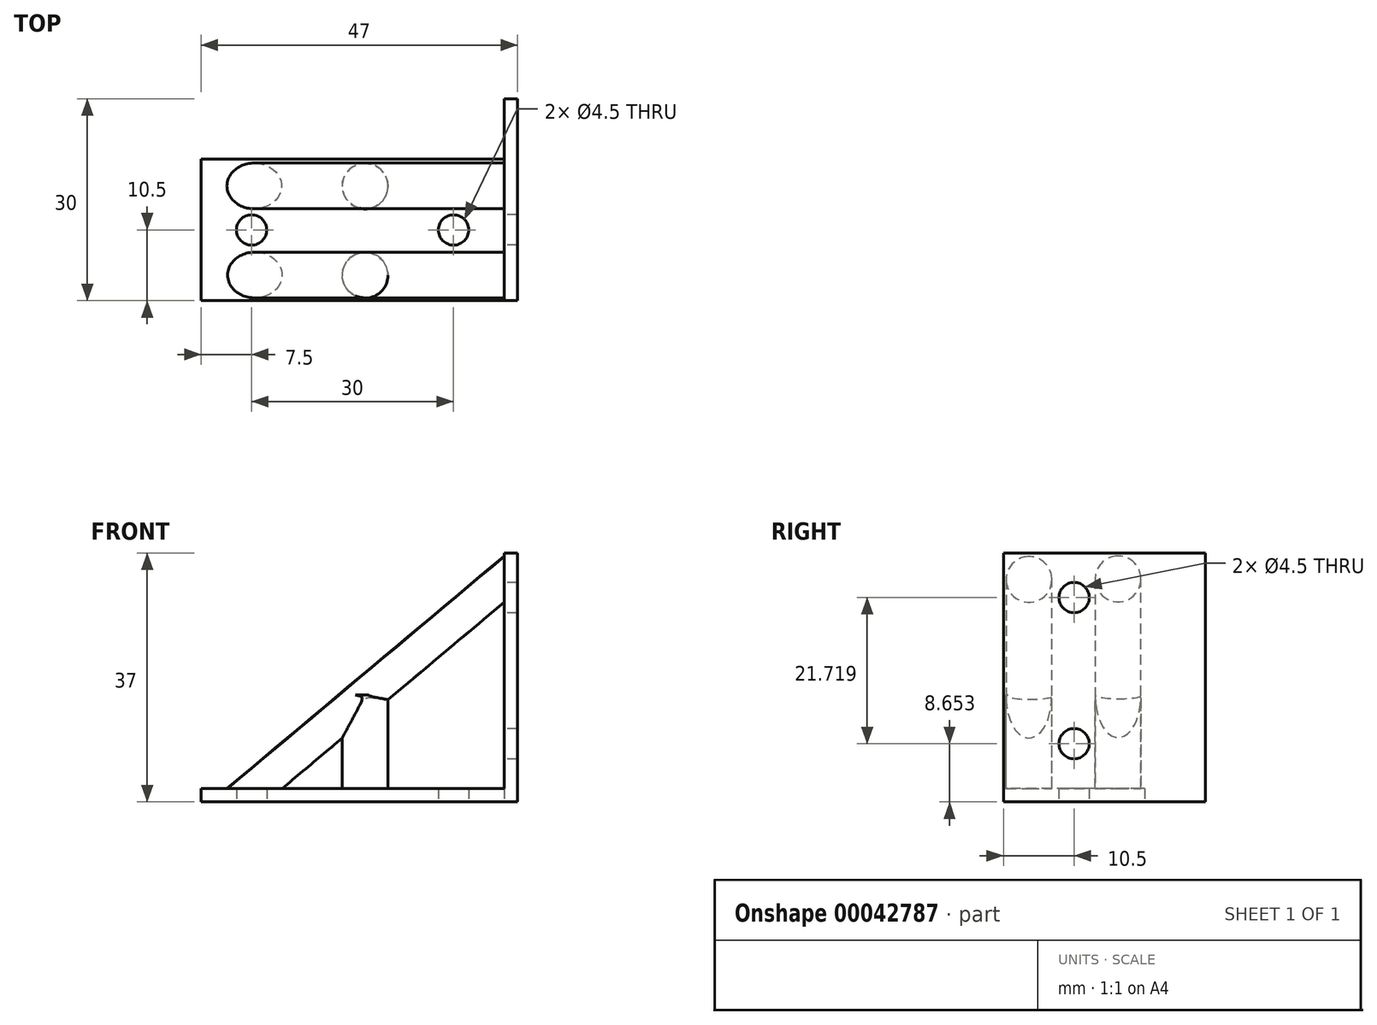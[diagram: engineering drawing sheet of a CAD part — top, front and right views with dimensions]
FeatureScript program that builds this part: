
annotation { "Feature Type Name" : "Feature", "Feature Type Description" : "" }
export const myFeature = defineFeature(function(context is Context, id is Id, definition is map)
    precondition{}
    {
        {
            var Q0;
            Q0=qCreatedBy(makeId("Top.planeOp"),FACE);
            var sketch = newSketch(context, id + "F0", { "sketchPlane" : qUnion([Q0])});
            skLineSegment(sketch, "E0.rect.bottom", {"start": v(-22.5, 10.5) * mm, "end": v(22.5, 10.5) * mm});
            skLineSegment(sketch, "E0.rect.top", {"start": v(-22.5, -10.5) * mm, "end": v(22.5, -10.5) * mm});
            skLineSegment(sketch, "E0.rect.left", {"start": v(-22.5, 10.5) * mm, "end": v(-22.5, -10.5) * mm});
            skLineSegment(sketch, "E0.rect.right", {"start": v(22.5, 10.5) * mm, "end": v(22.5, -10.5) * mm});
            skPoint(sketch, "E0.rect.middle", {"position": v(0, 0) * mm});
            skLineSegment(sketch, "E1.bottom", {"start": v(22.5, -10.5) * mm, "end": v(24.5, -10.5) * mm});
            skLineSegment(sketch, "E1.top", {"start": v(22.5, 19.5) * mm, "end": v(24.5, 19.5) * mm});
            skLineSegment(sketch, "E1.left", {"start": v(22.5, -10.5) * mm, "end": v(22.5, 19.5) * mm});
            skLineSegment(sketch, "E1.right", {"start": v(24.5, -10.5) * mm, "end": v(24.5, 19.5) * mm});
            skCircle(sketch, "E2", {"center": v(-15, 0) * mm, "radius": 2.25 * mm});
            skCircle(sketch, "E3", {"center": v(15, 0) * mm, "radius": 2.25 * mm});
            skSolve(sketch);
        }
        {
            var Q0;
            {var subQ0=sQuery(id+"F0.wireOp",EDGE,"E0.rect.bottom");Q0=makeQuery(id+"F0.imprint","IMPRINT",FACE,{"disambiguationData":[TD([[makeQuery(id+"F0.imprint","IMPRINT",EDGE,{"derivedFrom":subQ0}),-1.0]])]});}
            extrude(context, id + "F1", {"entities" : qUnion([Q0]), "depth" : 2 * mm});
        }
        {
            var Q0;
            {var subQ0=sQuery(id+"F0.wireOp",EDGE,"E1.bottom");Q0=makeQuery(id+"F0.imprint","IMPRINT",FACE,{"disambiguationData":[TD([[makeQuery(id+"F0.imprint","IMPRINT",EDGE,{"derivedFrom":subQ0}),1.0]])]});}
            extrude(context, id + "F2", {"entities" : qUnion([Q0]), "operationType" : NewBodyOperationType.ADD, "depth" : 37 * mm});
        }
        {
            var Q0;
            Q0=makeQuery(id+"F2.opExtrude","SWEPT_FACE",FACE,{"disambiguationData":[OSD([sQuery(id+"F0.wireOp",EDGE,"E1.left")])]});
            var sketch = newSketch(context, id + "F3", { "sketchPlane" : qUnion([Q0])});
            skPoint(sketch, "E4", {"position": v(0, 30.37) * mm});
            skPoint(sketch, "E5", {"position": v(0, 8.65) * mm});
            skCircle(sketch, "E6", {"center": v(0, 30.37) * mm, "radius": 2.25 * mm});
            skCircle(sketch, "E7", {"center": v(0, 8.65) * mm, "radius": 2.25 * mm});
            skLineSegment(sketch, "E8", {"start": v(0, 0) * mm, "end": v(0, 37) * mm, "construction": true});
            skSolve(sketch);
        }
        {
            var Q0;
            Q0=makeQuery(id+"F3.imprint","IMPRINT",FACE,{"disambiguationData":[TD([[makeQuery(id+"F3.imprint","IMPRINT",EDGE,{"derivedFrom":sQuery(id+"F3.wireOp",EDGE,"E6")}),1.0]])]});
            extrude(context, id + "F4", {"entities" : qUnion([Q0]), "operationType" : NewBodyOperationType.REMOVE, "oppositeDirection" : true, "depth" : 2 * mm});
        }
        {
            var Q0;
            Q0=makeQuery(id+"F3.imprint","IMPRINT",FACE,{"disambiguationData":[TD([[makeQuery(id+"F3.imprint","IMPRINT",EDGE,{"derivedFrom":sQuery(id+"F3.wireOp",EDGE,"E7")}),1.0]])]});
            extrude(context, id + "F5", {"entities" : qUnion([Q0]), "operationType" : NewBodyOperationType.REMOVE, "oppositeDirection" : true, "depth" : 2 * mm});
        }
        {
            var Q0;
            Q0=makeQuery(id+"F3.imprint","IMPRINT",FACE,{"disambiguationData":[TD([[makeQuery(id+"F3.imprint","IMPRINT",EDGE,{"derivedFrom":sQuery(id+"F3.wireOp",EDGE,"E6")}),-1.0]])]});
            var sketch = newSketch(context, id + "F6", { "sketchPlane" : qUnion([Q0])});
            skLineSegment(sketch, "E9", {"start": v(0, 0) * mm, "end": v(-9.48, 0) * mm, "construction": true});
            skLineSegment(sketch, "E10", {"start": v(0, 0) * mm, "end": v(-10.34, 0) * mm, "construction": true});
            skPoint(sketch, "E11", {"position": v(-5.17, 0) * mm});
            skLineSegment(sketch, "E12", {"start": v(0, 0) * mm, "end": v(13.4, 0) * mm, "construction": true});
            skPoint(sketch, "E13", {"position": v(6.7, 0) * mm});
            skLineSegment(sketch, "E14", {"start": v(-5.17, 0) * mm, "end": v(-5.17, 36.29) * mm, "construction": true});
            skLineSegment(sketch, "E15", {"start": v(6.7, 0) * mm, "end": v(6.7, 36.24) * mm, "construction": true});
            skCircle(sketch, "E16", {"center": v(6.7, 33.06) * mm, "radius": 3.4 * mm});
            skLineSegment(sketch, "E17", {"start": v(6.7, 33.06) * mm, "end": v(-5.17, 33.06) * mm, "construction": true});
            skCircle(sketch, "E18", {"center": v(-6.54, 33.14) * mm, "radius": 3.4 * mm});
            skLineSegment(sketch, "E19", {"start": v(-10.34, 36.97) * mm, "end": v(-10.34, 0) * mm, "construction": true});
            skSolve(sketch);
        }
        {
            var Q0;
            Q0=sQuery(id+"F6.wireOp",EDGE,"E17");
            cPlane(context, id + "F7", {"entities" : qUnion([Q0]), "cplaneType" : CPlaneType.LINE_ANGLE, "offset" : 150 * mm, "angle" : 140 * degree, "width" : 150 * mm, "height" : 150 * mm});
        }
        {
            var Q0;
            Q0=qCreatedBy(id+"F7.planeOp",FACE);
            var sketch = newSketch(context, id + "F8", { "sketchPlane" : qUnion([Q0])});
            skLineSegment(sketch, "E20", {"start": v(38.49, -5.2) * mm, "end": v(-16.5, -5.2) * mm});
            skLineSegment(sketch, "E21", {"start": v(38.46, 5.1) * mm, "end": v(-16.83, 5.1) * mm});
            skSolve(sketch);
        }
        {
            var Q0;
            Q0=makeQuery(id+"F6.imprint","IMPRINT",FACE,{"disambiguationData":[TD([[makeQuery(id+"F6.imprint","IMPRINT",EDGE,{"derivedFrom":sQuery(id+"F6.wireOp",EDGE,"E18")}),1.0]])]});
            var Q1;
            Q1=makeQuery(id+"F6.imprint","IMPRINT",FACE,{"disambiguationData":[TD([[makeQuery(id+"F6.imprint","IMPRINT",EDGE,{"derivedFrom":sQuery(id+"F6.wireOp",EDGE,"E16")}),1.0]])]});
            var Q2;
            Q2=sQuery(id+"F8.wireOp",EDGE,"E20");
            sweep(context, id + "F9", {"operationType" : NewBodyOperationType.ADD, "profiles" : qUnion([Q0, Q1]), "path" : qUnion([Q2])});
        }
        {
            var Q0;
            {var subQ0=sQuery(id+"F0.wireOp",EDGE,"E0.rect.bottom");Q0=makeQuery(id+"F0.imprint","IMPRINT",FACE,{"disambiguationData":[TD([[makeQuery(id+"F0.imprint","IMPRINT",EDGE,{"derivedFrom":subQ0}),-1.0]])]});}
            extrude(context, id + "F10", {"entities" : qUnion([Q0]), "operationType" : NewBodyOperationType.REMOVE, "oppositeDirection" : true, "depth" : 25.3 * mm});
        }
        {
            var Q0;
            Q0=makeQuery(id+"F1.opExtrude","CAP_FACE",FACE,{"disambiguationData":[OSD([sQuery(id+"F0.wireOp",EDGE,"E0.rect.bottom"),sQuery(id+"F0.wireOp",EDGE,"E0.rect.top"),sQuery(id+"F0.wireOp",EDGE,"E0.rect.left"),sQuery(id+"F0.wireOp",EDGE,"E1.left"),sQuery(id+"F0.wireOp",EDGE,"E2"),sQuery(id+"F0.wireOp",EDGE,"E3")])],"isStart":false});
            var sketch = newSketch(context, id + "F11", { "sketchPlane" : qUnion([Q0])});
            skPoint(sketch, "E22", {"position": v(-18.78, 10.5) * mm});
            skLineSegment(sketch, "E23", {"start": v(-18.78, 10.5) * mm, "end": v(22.5, 10.5) * mm, "construction": true});
            skPoint(sketch, "E24", {"position": v(1.86, 10.5) * mm});
            skLineSegment(sketch, "E25", {"start": v(1.86, 10.5) * mm, "end": v(1.86, -10.5) * mm, "construction": true});
            skPoint(sketch, "E26", {"position": v(1.86, 3.1) * mm});
            skPoint(sketch, "E27", {"position": v(1.86, 9.93) * mm});
            skPoint(sketch, "E28", {"position": v(1.86, -3.26) * mm});
            skPoint(sketch, "E29", {"position": v(1.86, -10.2) * mm});
            skLineSegment(sketch, "E30", {"start": v(1.86, -3.26) * mm, "end": v(1.86, -10.2) * mm, "construction": true});
            skLineSegment(sketch, "E31", {"start": v(1.86, -10.2) * mm, "end": v(1.86, -3.26) * mm, "construction": true});
            skPoint(sketch, "E32", {"position": v(1.86, -6.73) * mm});
            skLineSegment(sketch, "E33", {"start": v(1.86, 9.93) * mm, "end": v(1.86, 3.1) * mm, "construction": true});
            skPoint(sketch, "E34", {"position": v(1.86, 6.52) * mm});
            skCircle(sketch, "E35", {"center": v(1.86, 6.52) * mm, "radius": 3.4 * mm});
            skCircle(sketch, "E36", {"center": v(1.86, -6.73) * mm, "radius": 3.4 * mm});
            skSolve(sketch);
        }
        {
            var Q0;
            Q0=makeQuery(id+"F11.imprint","IMPRINT",FACE,{"disambiguationData":[TD([[makeQuery(id+"F11.imprint","IMPRINT",EDGE,{"derivedFrom":sQuery(id+"F11.wireOp",EDGE,"E35")}),1.0]])]});
            var Q1;
            Q1=sQuery(id+"F11.wireOp",EDGE,"E36");
            var Q2;
            Q2=sQuery(id+"F11.wireOp",EDGE,"E35");
            extrude(context, id + "F12", {"entities" : qUnion([Q0]), "operationType" : NewBodyOperationType.ADD, "surfaceEntities" : qUnion([Q1, Q2]), "depth" : 13.85 * mm});
        }
        {
            var Q0;
            Q0=makeQuery(id+"F11.imprint","IMPRINT",FACE,{"disambiguationData":[TD([[makeQuery(id+"F11.imprint","IMPRINT",EDGE,{"derivedFrom":sQuery(id+"F11.wireOp",EDGE,"E36")}),1.0]])]});
            var Q1;
            Q1=sQuery(id+"F11.wireOp",EDGE,"E36");
            extrude(context, id + "F13", {"entities" : qUnion([Q0]), "operationType" : NewBodyOperationType.ADD, "surfaceEntities" : qUnion([Q1]), "depth" : 13.9 * mm});
        }
    });
